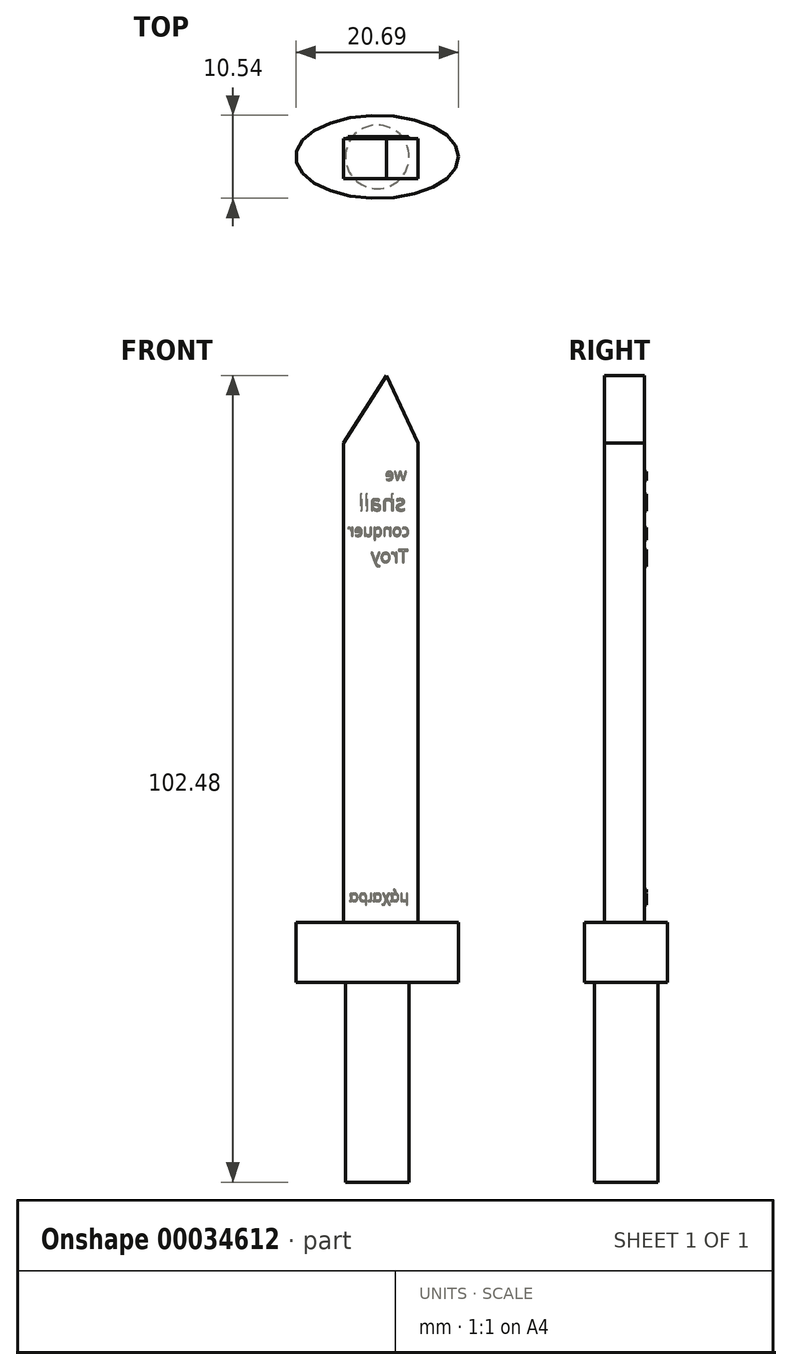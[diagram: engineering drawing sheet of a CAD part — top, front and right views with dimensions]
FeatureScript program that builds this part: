
annotation { "Feature Type Name" : "Feature", "Feature Type Description" : "" }
export const myFeature = defineFeature(function(context is Context, id is Id, definition is map)
    precondition{}
    {
        {
            var Q0;
            Q0=qCreatedBy(makeId("Front.planeOp"),FACE);
            var sketch = newSketch(context, id + "F0", { "sketchPlane" : qUnion([Q0])});
            skLineSegment(sketch, "E0.bottom", {"start": v(0, 0) * mm, "end": v(9.41, 0) * mm});
            skLineSegment(sketch, "E0.top", {"start": v(0, 60.9) * mm, "end": v(9.41, 60.9) * mm});
            skLineSegment(sketch, "E0.left", {"start": v(0, 0) * mm, "end": v(0, 60.9) * mm});
            skLineSegment(sketch, "E0.right", {"start": v(9.41, 0) * mm, "end": v(9.41, 60.9) * mm});
            skLineSegment(sketch, "E1", {"start": v(0, 60.9) * mm, "end": v(5.42, 69.46) * mm});
            skLineSegment(sketch, "E2", {"start": v(5.42, 69.46) * mm, "end": v(9.41, 60.9) * mm});
            skSolve(sketch);
        }
        {
            var Q0;
            Q0 = qSketchRegion(id + "F0", true);
            extrude(context, id + "F1", {"entities" : qUnion([Q0]), "depth" : 5.08 * mm});
        }
        {
            var Q0;
            Q0=makeQuery(id+"F1.opExtrude","SWEPT_FACE",FACE,{"disambiguationData":[OSD([sQuery(id+"F0.wireOp",EDGE,"E0.bottom")])]});
            var sketch = newSketch(context, id + "F2", { "sketchPlane" : qUnion([Q0])});
            skEllipse(sketch, "E3", {"center": v(4.26, 2.3) * mm, "majorRadius": 10.34 * mm, "minorRadius": 5.27 * mm, "majorAxis": v(1, 0)});
            skSolve(sketch);
        }
        {
            var Q0;
            Q0 = qSketchRegion(id + "F2", true);
            extrude(context, id + "F3", {"entities" : qUnion([Q0]), "operationType" : NewBodyOperationType.ADD, "depth" : 7.62 * mm});
        }
        {
            var Q0;
            Q0=makeQuery(id+"F3.opExtrude","CAP_FACE",FACE,{"disambiguationData":[OSD([sQuery(id+"F2.wireOp",EDGE,"E3")])],"isStart":false});
            var sketch = newSketch(context, id + "F4", { "sketchPlane" : qUnion([Q0])});
            skCircle(sketch, "E4", {"center": v(4.26, 2.3) * mm, "radius": 4.05 * mm});
            skSolve(sketch);
        }
        {
            var Q0;
            Q0=makeQuery(id+"F1.opExtrude","CAP_FACE",FACE,{"disambiguationData":[OSD([sQuery(id+"F0.wireOp",EDGE,"E0.bottom"),sQuery(id+"F0.wireOp",EDGE,"E0.left"),sQuery(id+"F0.wireOp",EDGE,"E0.right"),sQuery(id+"F0.wireOp",EDGE,"E1"),sQuery(id+"F0.wireOp",EDGE,"E2")])],"isStart":true});
            var sketch = newSketch(context, id + "F5", { "sketchPlane" : qUnion([Q0])});
            skText(sketch, "E5", { "text": "μάχαιρα\n", "fontName": "OpenSans-Regular.ttf"});
            skText(sketch, "E6", { "text": "we", "fontName": "OpenSans-Regular.ttf"});
            skText(sketch, "E7", { "text": "shall", "fontName": "OpenSans-Regular.ttf"});
            skText(sketch, "E8", { "text": "conquer", "fontName": "OpenSans-Regular.ttf"});
            skText(sketch, "E9", { "text": "Troy", "fontName": "OpenSans-Regular.ttf"});
            const initialGuessF5  = {"E5": [-0.00827, 0.00264, 1, 0, 0.00138], "E6": [-0.00798, 0.05615, 1, 0, 0.00147], "E7": [-0.00786, 0.05228, 1, 0, 0.002], "E8": [-0.00833, 0.04904, 1, 0, 0.00145], "E9": [-0.00821, 0.04571, 1, 0, 0.00165]};
            skSetInitialGuess(sketch, initialGuessF5);
            skSolve(sketch);
        }
        {
            var Q0;
            Q0 = qSketchRegion(id + "F5", true);
            extrude(context, id + "F6", {"entities" : qUnion([Q0]), "operationType" : NewBodyOperationType.ADD, "depth" : 0.25 * mm});
        }
        {
            var Q0;
            Q0 = qSketchRegion(id + "F5", true);
            extrude(context, id + "F7", {"entities" : qUnion([Q0]), "operationType" : NewBodyOperationType.ADD, "depth" : 0.25 * mm});
        }
        {
            var Q0;
            Q0=makeQuery(id+"F4.imprint","IMPRINT",FACE,{"disambiguationData":[TD([[makeQuery(id+"F4.imprint","IMPRINT",EDGE,{"derivedFrom":sQuery(id+"F4.wireOp",EDGE,"E4")}),1.0]])]});
            extrude(context, id + "F8", {"entities" : qUnion([Q0]), "operationType" : NewBodyOperationType.ADD, "depth" : 25.4 * mm});
        }
    });
